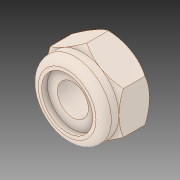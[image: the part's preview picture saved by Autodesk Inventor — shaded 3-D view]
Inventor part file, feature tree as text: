
AUTODESK INVENTOR PART (.ipt)
format: ipt  version: 2018 (Build 220112000, 112)  size: 135,168 bytes
history: native  units: in
note: dims shown in document units (in); Inventor stores cm internally (conversion verified against a paired STEP export)
features: fillet x1
ambient origin geometry x8: Origin, YZ Plane, XZ Plane, XY Plane, X Axis, Y Axis, Z Axis, Center Point
bodies: Solid1 (feature_tree)
feature tree (1):
  fillet  "Fillet1"  [1 undecoded]
note: 1 required parameter value undecoded (feature->parameter linkage not recoverable at this tier; creation-order binding heuristic only, values carry confidence <= 0.55)
